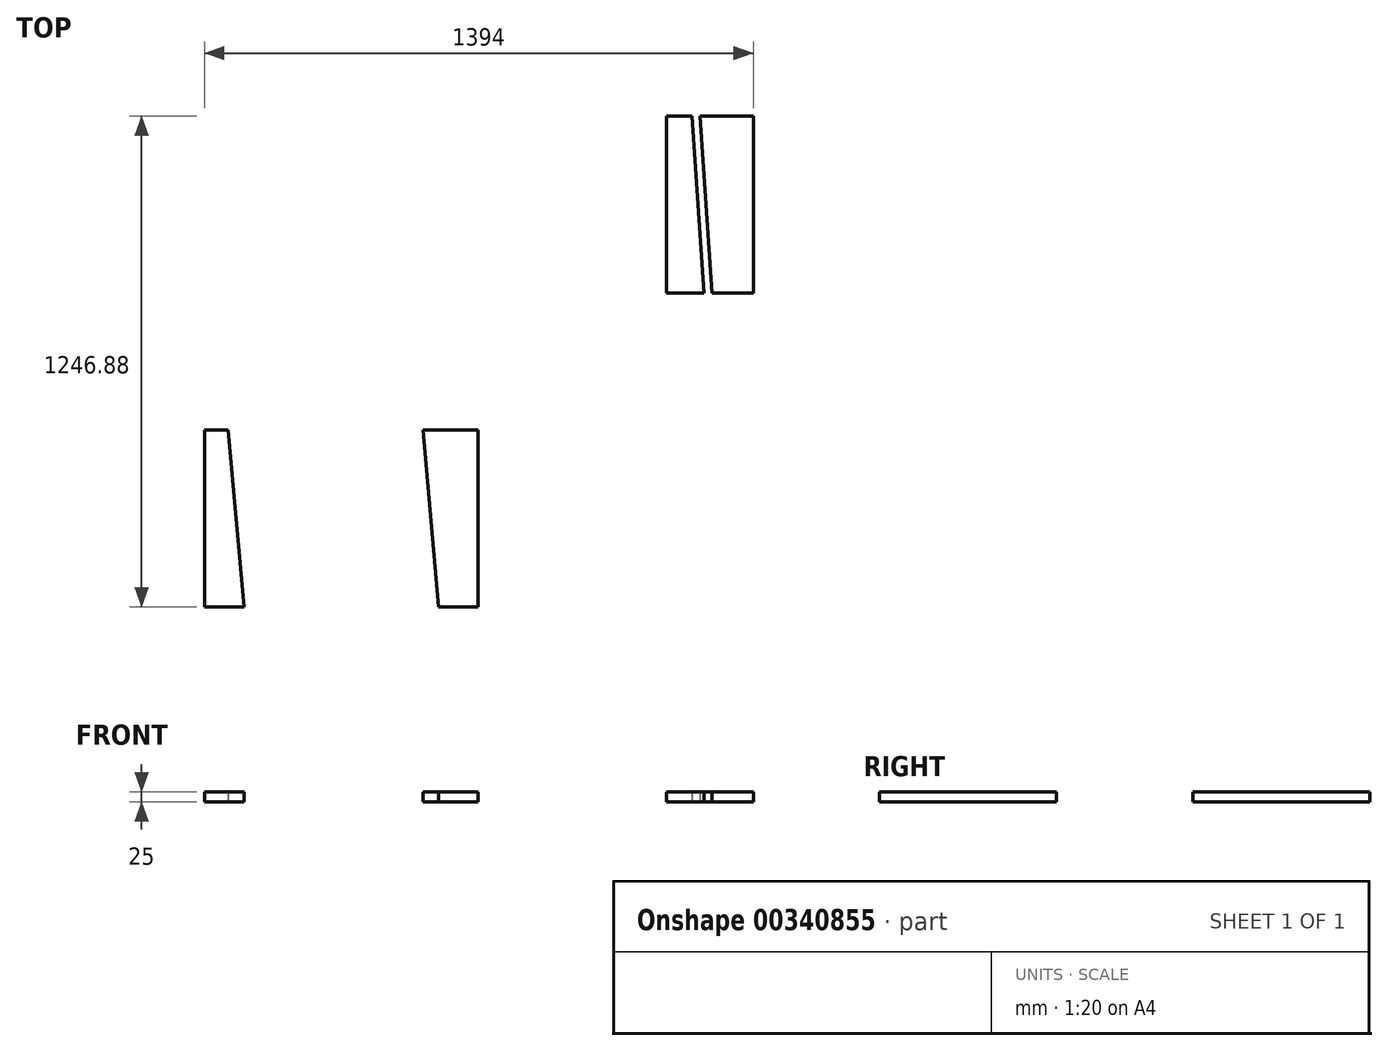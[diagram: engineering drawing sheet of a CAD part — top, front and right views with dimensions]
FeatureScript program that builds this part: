
annotation { "Feature Type Name" : "Feature", "Feature Type Description" : "" }
export const myFeature = defineFeature(function(context is Context, id is Id, definition is map)
    precondition{}
    {
        {
            var Q0;
            Q0=qCreatedBy(makeId("Top.planeOp"),FACE);
            var sketch = newSketch(context, id + "F0", { "sketchPlane" : qUnion([Q0])});
            skLineSegment(sketch, "E0", {"start": v(-2161.34, 1030.13) * mm, "end": v(-2161.34, 1480.13) * mm, "construction": true});
            skLineSegment(sketch, "E1", {"start": v(-2161.34, 1480.13) * mm, "end": v(-2096.34, 1480.13) * mm, "construction": true});
            skLineSegment(sketch, "E2", {"start": v(-2161.34, 1030.13) * mm, "end": v(-2066.34, 1030.13) * mm, "construction": true});
            skLineSegment(sketch, "E3", {"start": v(-2096.34, 1480.13) * mm, "end": v(-2066.34, 1030.13) * mm, "construction": true});
            skLineSegment(sketch, "E4", {"start": v(-2161.34, 1480.13) * mm, "end": v(-2161.34, 1030.13) * mm});
            skLineSegment(sketch, "E5", {"start": v(-2161.34, 1030.13) * mm, "end": v(-2066.34, 1030.13) * mm});
            skLineSegment(sketch, "E6", {"start": v(-2066.34, 1030.13) * mm, "end": v(-2096.34, 1480.13) * mm});
            skLineSegment(sketch, "E7", {"start": v(-2096.34, 1480.13) * mm, "end": v(-2161.34, 1480.13) * mm});
            skLineSegment(sketch, "E8", {"start": v(-1940.85, 1030.13) * mm, "end": v(-1940.85, 1480.13) * mm, "construction": true});
            skLineSegment(sketch, "E9", {"start": v(-2075.85, 1480.13) * mm, "end": v(-1940.85, 1480.13) * mm, "construction": true});
            skLineSegment(sketch, "E10", {"start": v(-2075.85, 1480.13) * mm, "end": v(-2045.85, 1030.13) * mm, "construction": true});
            skLineSegment(sketch, "E11", {"start": v(-2075.85, 1480.13) * mm, "end": v(-2045.85, 1030.13) * mm});
            skLineSegment(sketch, "E12", {"start": v(-2045.85, 1030.13) * mm, "end": v(-1940.85, 1030.13) * mm});
            skLineSegment(sketch, "E13", {"start": v(-1940.85, 1030.13) * mm, "end": v(-1940.85, 1480.13) * mm});
            skLineSegment(sketch, "E14", {"start": v(-2075.85, 1480.13) * mm, "end": v(-1940.85, 1480.13) * mm});
            skSolve(sketch);
        }
        {
            var Q0;
            Q0=makeQuery(id+"F0.imprint","IMPRINT",FACE,{"disambiguationData":[TD([[makeQuery(id+"F0.imprint","IMPRINT",EDGE,{"derivedFrom":sQuery(id+"F0.wireOp",EDGE,"E4")}),1.0]])]});
            var Q1;
            Q1=makeQuery(id+"F0.imprint","IMPRINT",FACE,{"disambiguationData":[TD([[makeQuery(id+"F0.imprint","IMPRINT",EDGE,{"derivedFrom":sQuery(id+"F0.wireOp",EDGE,"E11")}),1.0]])]});
            extrude(context, id + "F1", {"entities" : qUnion([Q0, Q1]), "depth" : 25 * mm});
        }
        {
            var Q0;
            Q0=qCreatedBy(makeId("Top.planeOp"),FACE);
            var sketch = newSketch(context, id + "F2", { "sketchPlane" : qUnion([Q0])});
            skLineSegment(sketch, "E15", {"start": v(-3134.85, 683.25) * mm, "end": v(-3274.85, 683.25) * mm, "construction": true});
            skLineSegment(sketch, "E16", {"start": v(-3274.85, 683.25) * mm, "end": v(-3334.85, 683.25) * mm, "construction": true});
            skLineSegment(sketch, "E17", {"start": v(-3334.85, 683.25) * mm, "end": v(-3334.85, 233.25) * mm, "construction": true});
            skLineSegment(sketch, "E18", {"start": v(-3334.85, 233.25) * mm, "end": v(-3234.85, 233.25) * mm, "construction": true});
            skLineSegment(sketch, "E19", {"start": v(-3234.85, 233.25) * mm, "end": v(-3134.85, 233.25) * mm, "construction": true});
            skLineSegment(sketch, "E20", {"start": v(-3134.85, 233.25) * mm, "end": v(-3134.85, 683.25) * mm, "construction": true});
            skLineSegment(sketch, "E21", {"start": v(-3234.85, 233.25) * mm, "end": v(-3274.85, 683.25) * mm, "construction": true});
            skLineSegment(sketch, "E22", {"start": v(-2640.01, 683.25) * mm, "end": v(-2780.01, 683.25) * mm, "construction": true});
            skLineSegment(sketch, "E23", {"start": v(-2780.01, 683.25) * mm, "end": v(-2840.01, 683.25) * mm, "construction": true});
            skLineSegment(sketch, "E24", {"start": v(-2840.01, 683.25) * mm, "end": v(-2840.01, 233.25) * mm, "construction": true});
            skLineSegment(sketch, "E25", {"start": v(-2840.01, 233.25) * mm, "end": v(-2740.01, 233.25) * mm, "construction": true});
            skLineSegment(sketch, "E26", {"start": v(-2740.01, 233.25) * mm, "end": v(-2640.01, 233.25) * mm, "construction": true});
            skLineSegment(sketch, "E27", {"start": v(-2640.01, 233.25) * mm, "end": v(-2640.01, 683.25) * mm, "construction": true});
            skLineSegment(sketch, "E28", {"start": v(-2740.01, 233.25) * mm, "end": v(-2780.01, 683.25) * mm, "construction": true});
            skLineSegment(sketch, "E29", {"start": v(-3274.85, 683.25) * mm, "end": v(-3334.85, 683.25) * mm});
            skLineSegment(sketch, "E30", {"start": v(-3334.85, 233.25) * mm, "end": v(-3334.85, 683.25) * mm});
            skLineSegment(sketch, "E31", {"start": v(-3274.85, 683.25) * mm, "end": v(-3234.85, 233.25) * mm});
            skLineSegment(sketch, "E32", {"start": v(-3234.85, 233.25) * mm, "end": v(-3334.85, 233.25) * mm});
            skLineSegment(sketch, "E33", {"start": v(-2780.01, 683.25) * mm, "end": v(-2640.01, 683.25) * mm});
            skLineSegment(sketch, "E34", {"start": v(-2640.01, 683.25) * mm, "end": v(-2640.01, 233.25) * mm});
            skLineSegment(sketch, "E35", {"start": v(-2640.01, 233.25) * mm, "end": v(-2740.01, 233.25) * mm});
            skLineSegment(sketch, "E36", {"start": v(-2740.01, 233.25) * mm, "end": v(-2780.01, 683.25) * mm});
            skSolve(sketch);
        }
        {
            var Q0;
            Q0=makeQuery(id+"F2.imprint","IMPRINT",FACE,{"disambiguationData":[TD([[makeQuery(id+"F2.imprint","IMPRINT",EDGE,{"derivedFrom":sQuery(id+"F2.wireOp",EDGE,"E33")}),-1.0]])]});
            var Q1;
            Q1=makeQuery(id+"F2.imprint","IMPRINT",FACE,{"disambiguationData":[TD([[makeQuery(id+"F2.imprint","IMPRINT",EDGE,{"derivedFrom":sQuery(id+"F2.wireOp",EDGE,"E29")}),1.0]])]});
            extrude(context, id + "F3", {"entities" : qUnion([Q0, Q1]), "depth" : 25 * mm});
        }
    });
